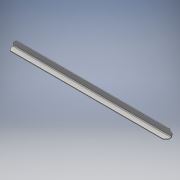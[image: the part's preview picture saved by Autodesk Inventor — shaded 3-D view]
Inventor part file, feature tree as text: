
AUTODESK INVENTOR PART (.ipt)
format: ipt  version: 2016 (Build 200138000, 138)  size: 120,832 bytes
history: native  units: mm
features: sheet_metal_op x4, other x3, sketch x2
ambient origin geometry x8: Origin, YZ Plane, XZ Plane, XY Plane, X Axis, Y Axis, Z Axis, Center Point
bodies: Solid1 (feature_tree)
feature tree (9):
  sheet_metal_op  "Face1"
  sheet_metal_op  "Flange1"
  other  "Corner Chamfer1"
  sketch  "Sketch1"  dims[d0=250.0mm]
  other  "Plate1"
  sketch  "Sketch2"  dims[d1=10.0mm d2=1.0mm d3=1.0mm d4=0.5mm d5=2.0mm d6=1.0mm d7=10.0mm d8=90.0deg d9=1.0mm d10=4.0mm d11=1.0mm d12=1.0mm d13=4.0mm d14=6.0mm d15=45.0deg]
  other  "Plate2"
  sheet_metal_op  "Bend1"
  sheet_metal_op  "Corner1"
